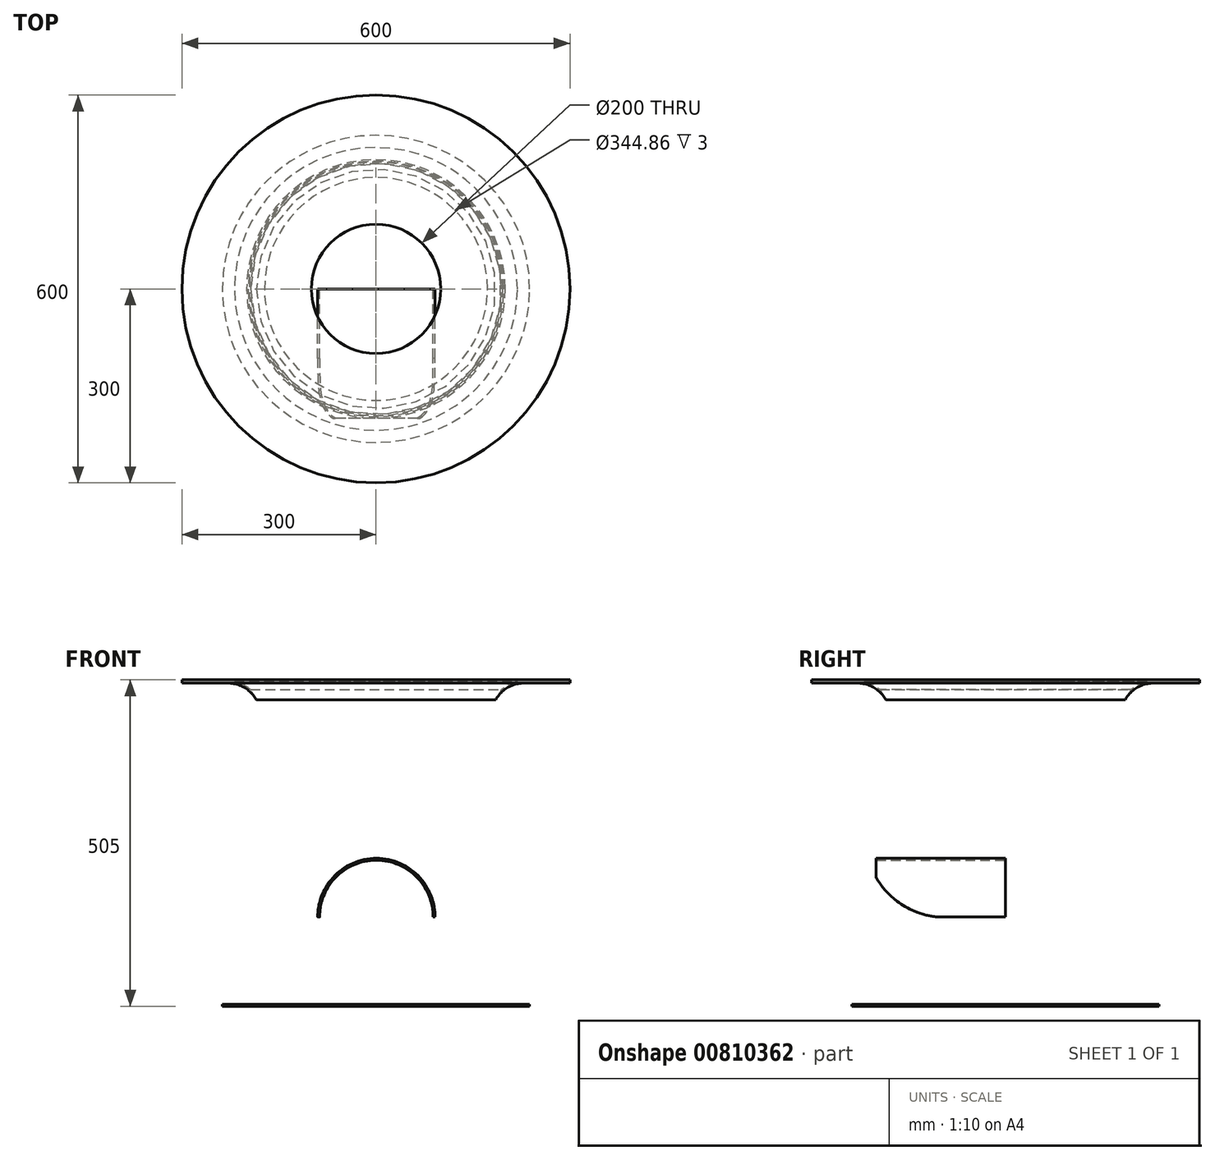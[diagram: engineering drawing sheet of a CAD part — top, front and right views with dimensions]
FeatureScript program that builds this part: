
annotation { "Feature Type Name" : "Feature", "Feature Type Description" : "" }
export const myFeature = defineFeature(function(context is Context, id is Id, definition is map)
    precondition{}
    {
        {
            var Q0;
            Q0=qCreatedBy(makeId("Front.planeOp"),FACE);
            var sketch = newSketch(context, id + "F0", { "sketchPlane" : qUnion([Q0])});
            skLineSegment(sketch, "E0", {"start": v(0, 0) * mm, "end": v(200, 0) * mm});
            skLineSegment(sketch, "E1", {"start": v(200, 0) * mm, "end": v(200, 505) * mm});
            skPoint(sketch, "E1.startSnap0", {"position": v(200, 0) * mm});
            skLineSegment(sketch, "E2", {"start": v(-100, 500) * mm, "end": v(-28.95, 500) * mm});
            skFitSpline(sketch, "E3", {"points": [v(0, 0) * mm, v(83.57, 267.3) * mm, v(0, 500) * mm], "startDerivative": vector(495.34, 620.54) * mm, "endDerivative": vector(-287.12, 476.11) * mm});
            skLineSegment(sketch, "E4.0.1.0", {"start": v(-100, 505) * mm, "end": v(100, 505) * mm});
            skLineSegment(sketch, "E4.direction2", {"start": v(-100, 500) * mm, "end": v(-100, 505) * mm, "construction": true});
            skArc(sketch, "E5.filletArc", {"start": v(14.97, 473.9) * mm, "mid": v(-3.4, 492.98) * mm, "end": v(-28.95, 500) * mm});
            skPoint(sketch, "E6.visualSharp", {"position": v(400, 500) * mm});
            skPoint(sketch, "E7.MirrorCS.start.orphan", {"position": v(400, 0) * mm});
            skPoint(sketch, "E8.trimOffspring.end.orphan", {"position": v(500, 490.1) * mm});
            skPoint(sketch, "E9.orphan", {"position": v(200, -192.3) * mm});
            skLineSegment(sketch, "E10", {"start": v(-100, 505) * mm, "end": v(-100, 500) * mm});
            skLineSegment(sketch, "E11.0", {"start": v(-18.7, 502) * mm, "end": v(100, 502) * mm});
            skArc(sketch, "E11.1", {"start": v(17.6, 475.33) * mm, "mid": v(2.42, 492.72) * mm, "end": v(-18.7, 502) * mm});
            skLineSegment(sketch, "E11.3", {"start": v(6.2, 3) * mm, "end": v(197, 3) * mm});
            skFitSpline(sketch, "E11.4", {"points": [v(2.34, -1.87) * mm, v(23.08, 24.1) * mm, v(55.61, 72.85) * mm, v(77.91, 128) * mm, v(87.08, 169.85) * mm, v(90.23, 200.42) * mm, v(90.25, 225.44) * mm, v(89.01, 245.34) * mm, v(87.78, 257.76) * mm, v(86.56, 267.7) * mm, v(85.2, 277.67) * mm, v(83.22, 290.17) * mm, v(80.41, 305.2) * mm, v(76.08, 325.3) * mm, v(69.54, 350.5) * mm, v(59.9, 380.82) * mm, v(48.44, 411.15) * mm, v(30.7, 451.51) * mm, v(14.58, 481.63) * mm, v(2.57, 501.55) * mm]});
            skLineSegment(sketch, "E12", {"start": v(100, 505) * mm, "end": v(100, 502) * mm});
            skLineSegment(sketch, "E13", {"start": v(0, 0) * mm, "end": v(-37.62, 0) * mm});
            skLineSegment(sketch, "E14", {"start": v(-37.62, 0) * mm, "end": v(-37.62, 3) * mm});
            skLineSegment(sketch, "E15", {"start": v(-37.62, 3) * mm, "end": v(2.38, 3) * mm});
            skLineSegment(sketch, "E16", {"start": v(27.57, 3) * mm, "end": v(27.57, 0) * mm});
            skSolve(sketch);
        }
        {
            var Q0;
            Q0 = qSketchRegion(id + "F0", true);
            var Q1;
            Q1=sQuery(id+"F0.wireOp",EDGE,"E1");
            revolve(context, id + "F1", {"surfaceOperationType" : NewSurfaceOperationType.NEW, "entities" : qUnion([Q0]), "axis" : qUnion([Q1]), "revolveType" : RevolveType.FULL});
        }
        {
            var Q0;
            Q0=qCreatedBy(makeId("Front.planeOp"),FACE);
            var sketch = newSketch(context, id + "F2", { "sketchPlane" : qUnion([Q0])});
            skCircle(sketch, "E17", {"center": v(200.6, 138.12) * mm, "radius": 87.5 * mm});
            skSolve(sketch);
        }
        {
            var Q0;
            Q0 = qSketchRegion(id + "F2", true);
            extrude(context, id + "F3", {"entities" : qUnion([Q0]), "operationType" : NewBodyOperationType.REMOVE, "endBound" : BoundingType.THROUGH_ALL, "depth" : 25 * mm, "offsetDistance" : 25 * mm});
        }
        {
            var Q0;
            Q0=qCreatedBy(makeId("Front.planeOp"),FACE);
            var sketch = newSketch(context, id + "F4", { "sketchPlane" : qUnion([Q0])});
            skArc(sketch, "E18", {"start": v(291.34, 138.12) * mm, "mid": v(200.59, 228.87) * mm, "end": v(109.84, 138.12) * mm});
            skArc(sketch, "E19.0", {"start": v(288.34, 138.12) * mm, "mid": v(200.59, 225.87) * mm, "end": v(112.84, 138.12) * mm});
            skLineSegment(sketch, "E20", {"start": v(291.34, 138.12) * mm, "end": v(288.34, 138.12) * mm});
            skPoint(sketch, "E21.orphan", {"position": v(360.8, 138.12) * mm});
            skLineSegment(sketch, "E22.trimOffspring", {"start": v(112.84, 138.12) * mm, "end": v(109.84, 138.12) * mm});
            skSolve(sketch);
        }
        {
            var Q0;
            Q0 = qSketchRegion(id + "F4", true);
            extrude(context, id + "F5", {"entities" : qUnion([Q0]), "operationType" : NewBodyOperationType.ADD, "depth" : 200 * mm, "offsetDistance" : 25 * mm});
        }
        {
            var Q0;
            Q0=qCreatedBy(makeId("Right.planeOp"),FACE);
            var sketch = newSketch(context, id + "F6", { "sketchPlane" : qUnion([Q0])});
            skArc(sketch, "E23", {"start": v(-199.64, 198.57) * mm, "mid": v(-160.67, 157.57) * mm, "end": v(-107.49, 138.27) * mm});
            skLineSegment(sketch, "E24", {"start": v(-199.64, 198.57) * mm, "end": v(-268.44, 198.57) * mm});
            skLineSegment(sketch, "E25", {"start": v(-268.44, 198.57) * mm, "end": v(-248.48, 116.18) * mm});
            skLineSegment(sketch, "E26", {"start": v(-248.48, 116.18) * mm, "end": v(-126.6, 112.36) * mm});
            skLineSegment(sketch, "E27", {"start": v(-126.6, 112.36) * mm, "end": v(-107.49, 138.27) * mm});
            skSolve(sketch);
        }
        {
            var Q0;
            Q0 = qSketchRegion(id + "F6", true);
            extrude(context, id + "F7", {"entities" : qUnion([Q0]), "operationType" : NewBodyOperationType.REMOVE, "endBound" : BoundingType.THROUGH_ALL, "depth" : 25 * mm, "offsetDistance" : 25 * mm});
        }
    });
